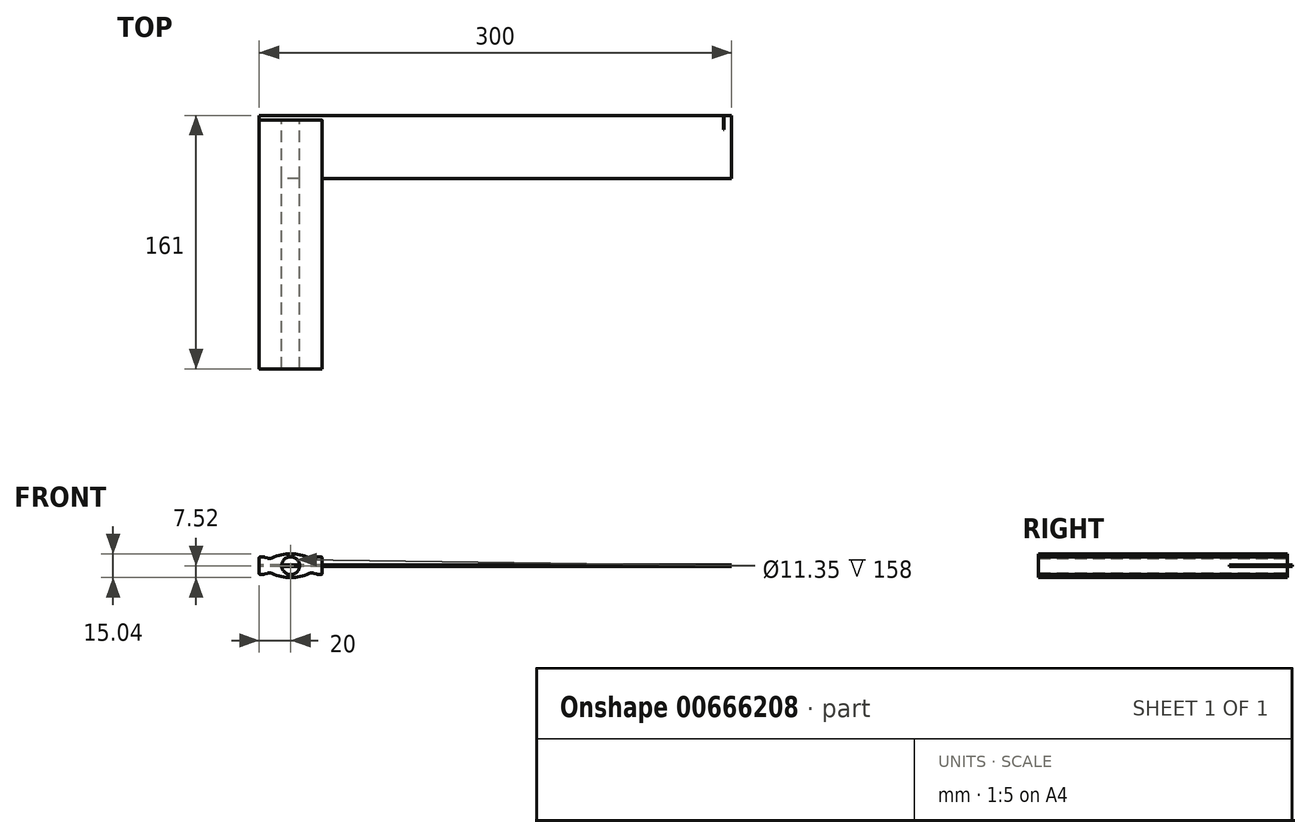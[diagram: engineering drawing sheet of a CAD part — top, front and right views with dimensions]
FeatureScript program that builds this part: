
annotation { "Feature Type Name" : "Feature", "Feature Type Description" : "" }
export const myFeature = defineFeature(function(context is Context, id is Id, definition is map)
    precondition{}
    {
        {
            var Q0;
            Q0=qCreatedBy(makeId("Front.planeOp"),FACE);
            var sketch = newSketch(context, id + "F0", { "sketchPlane" : qUnion([Q0])});
            skLineSegment(sketch, "E0.bottom", {"start": v(19.5, -5.5) * mm, "end": v(17.63, -5.5) * mm});
            skLineSegment(sketch, "E0.top", {"start": v(19.5, 5.5) * mm, "end": v(17.63, 5.5) * mm});
            skLineSegment(sketch, "E0.left", {"start": v(20, -5) * mm, "end": v(20, 5) * mm});
            skLineSegment(sketch, "E0.right", {"start": v(-20, -5) * mm, "end": v(-20, 5) * mm});
            skPoint(sketch, "E0.middle", {"position": v(0, 0) * mm});
            skLineSegment(sketch, "E1", {"start": v(-16.4, 5.3) * mm, "end": v(-14.73, 4.77) * mm});
            skLineSegment(sketch, "E2.MirrorCS", {"start": v(-16.4, -5.3) * mm, "end": v(-14.73, -4.77) * mm});
            skLineSegment(sketch, "E3.MirrorCS", {"start": v(16.4, 5.3) * mm, "end": v(14.73, 4.77) * mm});
            skLineSegment(sketch, "E4.MirrorCS", {"start": v(16.4, -5.3) * mm, "end": v(14.73, -4.77) * mm});
            skArc(sketch, "E5", {"start": v(11.83, 4.94) * mm, "mid": v(0, 7.52) * mm, "end": v(-11.83, 4.94) * mm});
            skArc(sketch, "E6.MirrorCS", {"start": v(11.83, -4.94) * mm, "mid": v(0, -7.52) * mm, "end": v(-11.83, -4.94) * mm});
            skPoint(sketch, "E7.visualSharp", {"position": v(-20, 5.5) * mm});
            skArc(sketch, "E7.filletArc", {"start": v(-19.5, 5.5) * mm, "mid": v(-19.85, 5.35) * mm, "end": v(-20, 5) * mm});
            skPoint(sketch, "E8.visualSharp", {"position": v(-20, -5.5) * mm});
            skArc(sketch, "E8.filletArc", {"start": v(-20, -5) * mm, "mid": v(-19.85, -5.35) * mm, "end": v(-19.5, -5.5) * mm});
            skPoint(sketch, "E9.visualSharp", {"position": v(20, 5.5) * mm});
            skArc(sketch, "E9.filletArc", {"start": v(20, 5) * mm, "mid": v(19.85, 5.35) * mm, "end": v(19.5, 5.5) * mm});
            skPoint(sketch, "E10.visualSharp", {"position": v(20, -5.5) * mm});
            skArc(sketch, "E10.filletArc", {"start": v(19.5, -5.5) * mm, "mid": v(19.85, -5.35) * mm, "end": v(20, -5) * mm});
            skLineSegment(sketch, "E11.trimOffspring", {"start": v(-17.63, -5.5) * mm, "end": v(-19.5, -5.5) * mm});
            skLineSegment(sketch, "E12.trimOffspring", {"start": v(-17.63, 5.5) * mm, "end": v(-19.5, 5.5) * mm});
            skPoint(sketch, "E13.visualSharp", {"position": v(-13.2, 4.27) * mm});
            skArc(sketch, "E13.filletArc", {"start": v(-14.73, 4.77) * mm, "mid": v(-13.27, 4.58) * mm, "end": v(-11.83, 4.94) * mm});
            skPoint(sketch, "E14.visualSharp", {"position": v(13.2, 4.27) * mm});
            skArc(sketch, "E14.filletArc", {"start": v(11.83, 4.94) * mm, "mid": v(13.27, 4.58) * mm, "end": v(14.73, 4.77) * mm});
            skPoint(sketch, "E15.visualSharp", {"position": v(13.2, -4.27) * mm});
            skArc(sketch, "E15.filletArc", {"start": v(14.73, -4.77) * mm, "mid": v(13.27, -4.58) * mm, "end": v(11.83, -4.94) * mm});
            skPoint(sketch, "E16.visualSharp", {"position": v(-13.2, -4.27) * mm});
            skArc(sketch, "E16.filletArc", {"start": v(-11.83, -4.94) * mm, "mid": v(-13.27, -4.58) * mm, "end": v(-14.73, -4.77) * mm});
            skPoint(sketch, "E17.visualSharp", {"position": v(-17, 5.5) * mm});
            skArc(sketch, "E17.filletArc", {"start": v(-16.4, 5.3) * mm, "mid": v(-17, 5.45) * mm, "end": v(-17.63, 5.5) * mm});
            skPoint(sketch, "E18.visualSharp", {"position": v(-17, -5.5) * mm});
            skArc(sketch, "E18.filletArc", {"start": v(-17.63, -5.5) * mm, "mid": v(-17, -5.45) * mm, "end": v(-16.4, -5.3) * mm});
            skPoint(sketch, "E19.visualSharp", {"position": v(17, -5.5) * mm});
            skArc(sketch, "E19.filletArc", {"start": v(16.4, -5.3) * mm, "mid": v(17, -5.45) * mm, "end": v(17.63, -5.5) * mm});
            skPoint(sketch, "E20.visualSharp", {"position": v(17, 5.5) * mm});
            skArc(sketch, "E20.filletArc", {"start": v(17.63, 5.5) * mm, "mid": v(17, 5.45) * mm, "end": v(16.4, 5.3) * mm});
            skCircle(sketch, "E21", {"center": v(0, 0) * mm, "radius": 5.68 * mm});
            skSolve(sketch);
        }
        {
            var Q0;
            Q0=makeQuery(id+"F0.imprint","IMPRINT",FACE,{"disambiguationData":[TD([[makeQuery(id+"F0.imprint","IMPRINT",EDGE,{"derivedFrom":sQuery(id+"F0.wireOp",EDGE,"E0.bottom")}),-1.0]])]});
            extrude(context, id + "F1", {"entities" : qUnion([Q0]), "depth" : 158 * mm, "offsetDistance" : 25 * mm});
        }
        {
            var Q0;
            Q0=makeQuery(id+"F1.opExtrude","SWEPT_FACE",FACE,{"disambiguationData":[OSD([sQuery(id+"F0.wireOp",EDGE,"E0.right")])]});
            var sketch = newSketch(context, id + "F2", { "sketchPlane" : qUnion([Q0])});
            skPoint(sketch, "E22.middle", {"position": v(0, 0) * mm});
            skLineSegment(sketch, "E23.bottom", {"start": v(37, -0.5) * mm, "end": v(-3, -0.5) * mm});
            skLineSegment(sketch, "E23.top", {"start": v(37, 0.5) * mm, "end": v(-3, 0.5) * mm});
            skLineSegment(sketch, "E23.left", {"start": v(37, -0.5) * mm, "end": v(37, 0.5) * mm});
            skLineSegment(sketch, "E23.right", {"start": v(-3, -0.5) * mm, "end": v(-3, 0.5) * mm});
            skPoint(sketch, "E23.middle", {"position": v(17, 0) * mm});
            skSolve(sketch);
        }
        {
            var Q0;
            {var subQ0=sQuery(id+"F2.wireOp",EDGE,"E23.right");Q0=makeQuery(id+"F2.imprint","IMPRINT",FACE,{"disambiguationData":[TD([[makeQuery(id+"F2.imprint","IMPRINT",EDGE,{"derivedFrom":subQ0}),-1.0]])]});}
            var Q1;
            {var subQ0=sQuery(id+"F2.wireOp",EDGE,"E23.left");Q1=makeQuery(id+"F2.imprint","IMPRINT",FACE,{"disambiguationData":[TD([[makeQuery(id+"F2.imprint","IMPRINT",EDGE,{"derivedFrom":subQ0}),1.0]])]});}
            extrude(context, id + "F3", {"entities" : qUnion([Q0, Q1]), "operationType" : NewBodyOperationType.ADD, "oppositeDirection" : true, "depth" : 300 * mm, "offsetDistance" : 25 * mm});
        }
        {
            var Q0;
            Q0=makeQuery(id+"F3.opExtrude","SWEPT_FACE",FACE,{"disambiguationData":[OSD([sQuery(id+"F2.wireOp",EDGE,"E23.top")])]});
            var sketch = newSketch(context, id + "F4", { "sketchPlane" : qUnion([Q0])});
            skLineSegment(sketch, "E24", {"start": v(274.95, 3) * mm, "end": v(274.95, -6) * mm});
            skLineSegment(sketch, "E25", {"start": v(274.95, -6) * mm, "end": v(275.25, -6) * mm});
            skLineSegment(sketch, "E26", {"start": v(275.25, -6) * mm, "end": v(275.25, 3) * mm});
            skLineSegment(sketch, "E27.0.1.0", {"start": v(274.95, -28) * mm, "end": v(274.95, -37) * mm});
            skLineSegment(sketch, "E27.1.0.0", {"start": v(269.95, 3) * mm, "end": v(269.95, -6) * mm});
            skLineSegment(sketch, "E27.1.1.0", {"start": v(269.95, -28) * mm, "end": v(269.95, -37) * mm});
            skLineSegment(sketch, "E27.2.0.0", {"start": v(264.95, 3) * mm, "end": v(264.95, -6) * mm});
            skLineSegment(sketch, "E27.2.1.0", {"start": v(264.95, -28) * mm, "end": v(264.95, -37) * mm});
            skLineSegment(sketch, "E27.direction1", {"start": v(274.95, -6) * mm, "end": v(269.95, -6) * mm, "construction": true});
            skLineSegment(sketch, "E27.direction2", {"start": v(274.95, -6) * mm, "end": v(274.95, -37) * mm, "construction": true});
            skLineSegment(sketch, "E28.0.3.0", {"start": v(259.95, 3) * mm, "end": v(259.95, -6) * mm});
            skLineSegment(sketch, "E28.0.3.1", {"start": v(259.95, -28) * mm, "end": v(259.95, -37) * mm});
            skLineSegment(sketch, "E28.0.4.0", {"start": v(254.95, 3) * mm, "end": v(254.95, -6) * mm});
            skLineSegment(sketch, "E28.0.4.1", {"start": v(254.95, -28) * mm, "end": v(254.95, -37) * mm});
            skLineSegment(sketch, "E28.0.5.0", {"start": v(249.95, 3) * mm, "end": v(249.95, -6) * mm});
            skLineSegment(sketch, "E28.0.5.1", {"start": v(249.95, -28) * mm, "end": v(249.95, -37) * mm});
            skLineSegment(sketch, "E28.0.6.0", {"start": v(244.95, 3) * mm, "end": v(244.95, -6) * mm});
            skLineSegment(sketch, "E28.0.6.1", {"start": v(244.95, -28) * mm, "end": v(244.95, -37) * mm});
            skLineSegment(sketch, "E28.0.7.0", {"start": v(239.95, 3) * mm, "end": v(239.95, -6) * mm});
            skLineSegment(sketch, "E28.0.7.1", {"start": v(239.95, -28) * mm, "end": v(239.95, -37) * mm});
            skLineSegment(sketch, "E29.0.8.0", {"start": v(234.95, 3) * mm, "end": v(234.95, -6) * mm});
            skLineSegment(sketch, "E29.0.8.1", {"start": v(234.95, -28) * mm, "end": v(234.95, -37) * mm});
            skLineSegment(sketch, "E29.0.9.0", {"start": v(229.95, 3) * mm, "end": v(229.95, -6) * mm});
            skLineSegment(sketch, "E29.0.9.1", {"start": v(229.95, -28) * mm, "end": v(229.95, -37) * mm});
            skLineSegment(sketch, "E29.0.10.0", {"start": v(224.95, 3) * mm, "end": v(224.95, -6) * mm});
            skLineSegment(sketch, "E29.0.10.1", {"start": v(224.95, -28) * mm, "end": v(224.95, -37) * mm});
            skLineSegment(sketch, "E29.0.11.0", {"start": v(219.95, 3) * mm, "end": v(219.95, -6) * mm});
            skLineSegment(sketch, "E29.0.11.1", {"start": v(219.95, -28) * mm, "end": v(219.95, -37) * mm});
            skLineSegment(sketch, "E29.0.12.0", {"start": v(214.95, 3) * mm, "end": v(214.95, -6) * mm});
            skLineSegment(sketch, "E29.0.12.1", {"start": v(214.95, -28) * mm, "end": v(214.95, -37) * mm});
            skLineSegment(sketch, "E29.0.13.0", {"start": v(209.95, 3) * mm, "end": v(209.95, -6) * mm});
            skLineSegment(sketch, "E29.0.13.1", {"start": v(209.95, -28) * mm, "end": v(209.95, -37) * mm});
            skLineSegment(sketch, "E29.0.14.0", {"start": v(204.95, 3) * mm, "end": v(204.95, -6) * mm});
            skLineSegment(sketch, "E29.0.14.1", {"start": v(204.95, -28) * mm, "end": v(204.95, -37) * mm});
            skLineSegment(sketch, "E29.0.15.0", {"start": v(199.95, 3) * mm, "end": v(199.95, -6) * mm});
            skLineSegment(sketch, "E29.0.15.1", {"start": v(199.95, -28) * mm, "end": v(199.95, -37) * mm});
            skLineSegment(sketch, "E29.0.16.0", {"start": v(194.95, 3) * mm, "end": v(194.95, -6) * mm});
            skLineSegment(sketch, "E29.0.16.1", {"start": v(194.95, -28) * mm, "end": v(194.95, -37) * mm});
            skLineSegment(sketch, "E29.0.17.0", {"start": v(189.95, 3) * mm, "end": v(189.95, -6) * mm});
            skLineSegment(sketch, "E29.0.17.1", {"start": v(189.95, -28) * mm, "end": v(189.95, -37) * mm});
            skLineSegment(sketch, "E29.0.18.0", {"start": v(184.95, 3) * mm, "end": v(184.95, -6) * mm});
            skLineSegment(sketch, "E29.0.18.1", {"start": v(184.95, -28) * mm, "end": v(184.95, -37) * mm});
            skLineSegment(sketch, "E29.0.19.0", {"start": v(179.95, 3) * mm, "end": v(179.95, -6) * mm});
            skLineSegment(sketch, "E29.0.19.1", {"start": v(179.95, -28) * mm, "end": v(179.95, -37) * mm});
            skLineSegment(sketch, "E29.0.20.0", {"start": v(174.95, 3) * mm, "end": v(174.95, -6) * mm});
            skLineSegment(sketch, "E29.0.20.1", {"start": v(174.95, -28) * mm, "end": v(174.95, -37) * mm});
            skLineSegment(sketch, "E29.0.21.0", {"start": v(169.95, 3) * mm, "end": v(169.95, -6) * mm});
            skLineSegment(sketch, "E29.0.21.1", {"start": v(169.95, -28) * mm, "end": v(169.95, -37) * mm});
            skLineSegment(sketch, "E29.0.22.0", {"start": v(164.95, 3) * mm, "end": v(164.95, -6) * mm});
            skLineSegment(sketch, "E29.0.22.1", {"start": v(164.95, -28) * mm, "end": v(164.95, -37) * mm});
            skLineSegment(sketch, "E29.0.23.0", {"start": v(159.95, 3) * mm, "end": v(159.95, -6) * mm});
            skLineSegment(sketch, "E29.0.23.1", {"start": v(159.95, -28) * mm, "end": v(159.95, -37) * mm});
            skLineSegment(sketch, "E29.0.24.0", {"start": v(154.95, 3) * mm, "end": v(154.95, -6) * mm});
            skLineSegment(sketch, "E29.0.24.1", {"start": v(154.95, -28) * mm, "end": v(154.95, -37) * mm});
            skLineSegment(sketch, "E29.0.25.0", {"start": v(149.95, 3) * mm, "end": v(149.95, -6) * mm});
            skLineSegment(sketch, "E29.0.25.1", {"start": v(149.95, -28) * mm, "end": v(149.95, -37) * mm});
            skLineSegment(sketch, "E29.0.26.0", {"start": v(144.95, 3) * mm, "end": v(144.95, -6) * mm});
            skLineSegment(sketch, "E29.0.26.1", {"start": v(144.95, -28) * mm, "end": v(144.95, -37) * mm});
            skLineSegment(sketch, "E29.0.27.0", {"start": v(139.95, 3) * mm, "end": v(139.95, -6) * mm});
            skLineSegment(sketch, "E29.0.27.1", {"start": v(139.95, -28) * mm, "end": v(139.95, -37) * mm});
            skLineSegment(sketch, "E29.0.28.0", {"start": v(134.95, 3) * mm, "end": v(134.95, -6) * mm});
            skLineSegment(sketch, "E29.0.28.1", {"start": v(134.95, -28) * mm, "end": v(134.95, -37) * mm});
            skLineSegment(sketch, "E29.0.29.0", {"start": v(129.95, 3) * mm, "end": v(129.95, -6) * mm});
            skLineSegment(sketch, "E29.0.29.1", {"start": v(129.95, -28) * mm, "end": v(129.95, -37) * mm});
            skLineSegment(sketch, "E29.0.30.0", {"start": v(124.95, 3) * mm, "end": v(124.95, -6) * mm});
            skLineSegment(sketch, "E29.0.30.1", {"start": v(124.95, -28) * mm, "end": v(124.95, -37) * mm});
            skLineSegment(sketch, "E29.0.31.0", {"start": v(119.95, 3) * mm, "end": v(119.95, -6) * mm});
            skLineSegment(sketch, "E29.0.31.1", {"start": v(119.95, -28) * mm, "end": v(119.95, -37) * mm});
            skLineSegment(sketch, "E29.0.32.0", {"start": v(114.95, 3) * mm, "end": v(114.95, -6) * mm});
            skLineSegment(sketch, "E29.0.32.1", {"start": v(114.95, -28) * mm, "end": v(114.95, -37) * mm});
            skLineSegment(sketch, "E29.0.33.0", {"start": v(109.95, 3) * mm, "end": v(109.95, -6) * mm});
            skLineSegment(sketch, "E29.0.33.1", {"start": v(109.95, -28) * mm, "end": v(109.95, -37) * mm});
            skLineSegment(sketch, "E29.0.34.0", {"start": v(104.95, 3) * mm, "end": v(104.95, -6) * mm});
            skLineSegment(sketch, "E29.0.34.1", {"start": v(104.95, -28) * mm, "end": v(104.95, -37) * mm});
            skLineSegment(sketch, "E29.0.35.0", {"start": v(99.95, 3) * mm, "end": v(99.95, -6) * mm});
            skLineSegment(sketch, "E29.0.35.1", {"start": v(99.95, -28) * mm, "end": v(99.95, -37) * mm});
            skLineSegment(sketch, "E29.0.36.0", {"start": v(94.95, 3) * mm, "end": v(94.95, -6) * mm});
            skLineSegment(sketch, "E29.0.36.1", {"start": v(94.95, -28) * mm, "end": v(94.95, -37) * mm});
            skLineSegment(sketch, "E29.0.37.0", {"start": v(89.95, 3) * mm, "end": v(89.95, -6) * mm});
            skLineSegment(sketch, "E29.0.37.1", {"start": v(89.95, -28) * mm, "end": v(89.95, -37) * mm});
            skLineSegment(sketch, "E29.0.38.0", {"start": v(84.95, 3) * mm, "end": v(84.95, -6) * mm});
            skLineSegment(sketch, "E29.0.38.1", {"start": v(84.95, -28) * mm, "end": v(84.95, -37) * mm});
            skLineSegment(sketch, "E29.0.39.0", {"start": v(79.95, 3) * mm, "end": v(79.95, -6) * mm});
            skLineSegment(sketch, "E29.0.39.1", {"start": v(79.95, -28) * mm, "end": v(79.95, -37) * mm});
            skLineSegment(sketch, "E30.0.40.0", {"start": v(74.95, 3) * mm, "end": v(74.95, -6) * mm});
            skLineSegment(sketch, "E30.0.40.1", {"start": v(74.95, -28) * mm, "end": v(74.95, -37) * mm});
            skLineSegment(sketch, "E30.0.41.0", {"start": v(69.95, 3) * mm, "end": v(69.95, -6) * mm});
            skLineSegment(sketch, "E30.0.41.1", {"start": v(69.95, -28) * mm, "end": v(69.95, -37) * mm});
            skLineSegment(sketch, "E30.0.42.0", {"start": v(64.95, 3) * mm, "end": v(64.95, -6) * mm});
            skLineSegment(sketch, "E30.0.42.1", {"start": v(64.95, -28) * mm, "end": v(64.95, -37) * mm});
            skLineSegment(sketch, "E30.0.43.0", {"start": v(59.95, 3) * mm, "end": v(59.95, -6) * mm});
            skLineSegment(sketch, "E30.0.43.1", {"start": v(59.95, -28) * mm, "end": v(59.95, -37) * mm});
            skLineSegment(sketch, "E30.0.44.0", {"start": v(54.95, 3) * mm, "end": v(54.95, -6) * mm});
            skLineSegment(sketch, "E30.0.44.1", {"start": v(54.95, -28) * mm, "end": v(54.95, -37) * mm});
            skLineSegment(sketch, "E30.0.45.0", {"start": v(49.95, 3) * mm, "end": v(49.95, -6) * mm});
            skLineSegment(sketch, "E30.0.45.1", {"start": v(49.95, -28) * mm, "end": v(49.95, -37) * mm});
            skLineSegment(sketch, "E30.0.46.0", {"start": v(44.95, 3) * mm, "end": v(44.95, -6) * mm});
            skLineSegment(sketch, "E30.0.46.1", {"start": v(44.95, -28) * mm, "end": v(44.95, -37) * mm});
            skLineSegment(sketch, "E30.0.47.0", {"start": v(39.95, 3) * mm, "end": v(39.95, -6) * mm});
            skLineSegment(sketch, "E30.0.47.1", {"start": v(39.95, -28) * mm, "end": v(39.95, -37) * mm});
            skLineSegment(sketch, "E30.0.48.0", {"start": v(34.95, 3) * mm, "end": v(34.95, -6) * mm});
            skLineSegment(sketch, "E30.0.48.1", {"start": v(34.95, -28) * mm, "end": v(34.95, -37) * mm});
            skLineSegment(sketch, "E30.0.49.0", {"start": v(29.95, 3) * mm, "end": v(29.95, -6) * mm});
            skLineSegment(sketch, "E30.0.49.1", {"start": v(29.95, -28) * mm, "end": v(29.95, -37) * mm});
            skLineSegment(sketch, "E30.0.50.0", {"start": v(24.95, 3) * mm, "end": v(24.95, -6) * mm});
            skLineSegment(sketch, "E30.0.50.1", {"start": v(24.95, -28) * mm, "end": v(24.95, -37) * mm});
            skSolve(sketch);
        }
        {
            var Q0;
            {var subQ0=sQuery(id+"F4.wireOp",EDGE,"E24");Q0=makeQuery(id+"F4.imprint","IMPRINT",FACE,{"disambiguationData":[TD([[makeQuery(id+"F4.imprint","IMPRINT",EDGE,{"derivedFrom":subQ0}),1.0]])]});}
            extrude(context, id + "F5", {"entities" : qUnion([Q0]), "operationType" : NewBodyOperationType.REMOVE, "oppositeDirection" : true, "depth" : 0.5 * mm, "offsetDistance" : 25 * mm});
        }
    });
